# Revit family: 09469179
name_source: partatom
category: Plumbing Fixtures
revit_build: Autodesk Revit 2018 (Build: 20170223_1515(x64)
units: mm (PartAtom-declared; Revit-internal decimal feet)

## family parameters
Always vertical = Yes
Cut with Voids When Loaded = No
OmniClass Number = 23.45.55.00
OmniClass Title = Sanitary Faucets, Wastes
Part Type = Normal
Room Calculation Point = No
Round Connector Dimension = Use Diameter
Shared = No
Work Plane-Based = No

## types (1)
- 09469179 Cover part for urinal flusher, 9/12 V, Bluetooth
    2D/3D/BIM Files URL = http://static.hansa.com
    3D View = https://static.hansa.com
    Advanced Features = Software settings adjustable via App
    Afterflush Period = 6 s (1-20 s)
    AssetType = Fixed
    Automatic Flush Frequency = 24 h (off/1-120 h)
    Automatic Flush Period = 6 s (1-120 s)
    BIMObjectName = 09469179
    Bluetooth = 4.x
    BodyMaterial = Brass
    Brand = HANSA
    Catalog Drawing URL = http://static.hansa.com
    Category = Bathroom;Public & Semi-public
    CloseOffRating = 0
    Color = Chrome
    Concealed Parts = Square rosette
    Dimension Drawing URL = http://static.hansa.com
    DurationUnit = Year
    EAN Number = 4057304014031
    EMC Directive = 2014/53/EU , 2011/65/EU
    EN Standard = EN 15091
    ETIM Class Number = EC010210 Electronic urinal flusher
    Electrical Connection = 12 V
    Electronic Parts = Autofocus infrared sensor;Solenoid valve
    FDV Document URL = http://www.hansa.com
    FaucetMainMaterial = Brass
    Features = Trim Kit;Touchless;Bluetooth®;External transformer
    Finish = Polished
    Flow Drawing URL = http://static.hansa.com
    Flow Rate At 300kPa = 0.2 L/s
    FlowCoefficient = 0
    Group = Urinal flusher
    IfcExportAs = IfcValveType
    IfcExportType = FAUCET
    InletConnectionSize = 10 mm  [stored 0.0328084 ft]
    Installation Type = Concealed wall mounting
    Installation and Maintenance Guide URL = http://static.hansa.com
    Interactive AR View URL = https://static.hansa.com
    Manufacturer = HANSA
    ManufacturerName = HANSA
    ManufacturerURL = http://www.hansa.com
    Market = International;Germany;Austria;Belgium;Netherlands;France;Czech Republic;Slovakia;Italy;Spain
    Material = Brass
    Max. Hot Water Supply = 70 °C
    Mobile Product Information URL = http://mpi.hansa.com
    Model = 09469179 Cover part for urinal flusher, 9/12 V, Bluetooth
    ModelReference = 09469179
    NBSDescription = Water supply fittings for baths
    NBSReference = 45-35-70/315
    Name = 09469179 Cover part for urinal flusher, 9/12 V, Bluetooth
    Name_en = 09469179 Cover part for urinal flusher, 9/12 V, Bluetooth
    NominalDepth = 12 mm  [stored 0.0393701 ft]
    NominalHeight = 140 mm  [stored 0.459318 ft]
    NominalWidth = 140 mm  [stored 0.459318 ft]
    Operating Distance = 150-400 mm (300/400/500 mm)
    Operating Voltage = 12 V
    Pre-flush Period = 2 s (OFF / 1-10 s)
    Product Code = 09469179
    Product Family = HANSAELECTRA
    Product Image URL = http://static.hansa.com
    Product URL = http://static.hansa.com
    Protection Class = IP 55
    Revision = 3
    Sales Package dimensions (LxWxH) = 210 x 165 x 60
    Shape = Sculptured
    Size = 12 x 140 x 140 mm
    Spare-Part Information URL = http://static.hansa.com
    Surface treatment = Chrome
    Technical DataSheet URL = http://www.hansa.com
    UNSPSC Class Number = 30181810 Faucet trim
    URL Declaration of Conformity = http://static.hansa.com
    URL REACH = http://static.hansa.com
    URL WEEE = http://www.hansa.com
    Uniclass2 = Pr_40_30_96_07
    Uniclass2015Description = Bath manual water supply sets
    Uniclass2015Reference = Pr_40_20_87_07
    Version = 3
    VersionDate = 01/07/2022
    Warranty Information URL = http://warranty.hansa.com
    WarrantyDescription = http://warranty.hansa.com
    WarrantyDurationUnit = Year
    Working Pressure = 50 - 1000 kPa
    WorkingPressure = 50 - 1000 kPa

note: [stored X ft] marks values corroborated as IEEE doubles in the binary element streams (Revit-internal decimal feet)

## geometry (parser evidence)
native form markers: Sweep x5
no freeform markers — native parametric forms only
